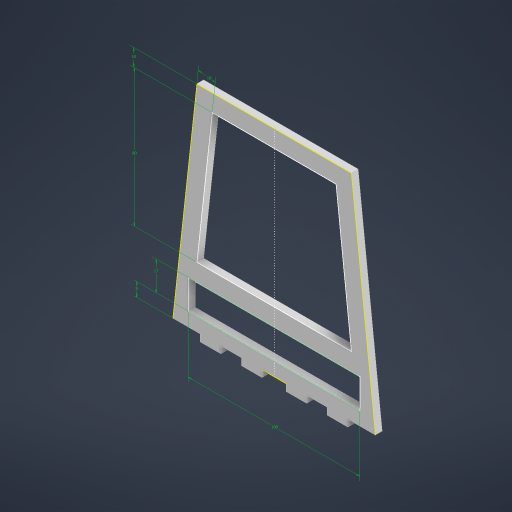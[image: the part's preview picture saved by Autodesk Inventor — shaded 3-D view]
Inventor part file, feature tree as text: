
AUTODESK INVENTOR PART (.ipt)
format: ipt  version: 2023.2 (Build 272271000, 271)  size: 274,944 bytes
history: native  units: mm
features: sketch x2
ambient origin geometry x8: Origin, YZ Plane, XZ Plane, XY Plane, X Axis, Y Axis, Z Axis, Center Point
bodies: Body1 (feature_tree)
feature tree (2):
  sketch  "Sketch1"  dims[d229=90.0mm]
  sketch  "Sketch2"  dims[d232=16.0mm d233=12.0mm d234=12.0mm d235=4.0mm d237=4.0mm d238=0.0mm d239=14.0mm d241=130.0mm d242=100.0mm d243=17.0mm d245=8.0mm d246=10.0mm d247=80.0mm d249=10.0mm d250=4.0mm d251=0.0mm d9=0.5mm d10=0.872665mm d11=0.5mm d12=0.872665mm d13=0.5mm d14=0.872665mm d27=0.5mm d28=0.872665mm d29=0.5mm d30=0.872665mm d88=0.5mm d89=0.872665mm d90=0.5mm d91=0.872665mm d116=0.5mm d117=0.872665mm d118=0.5mm d119=0.872665mm d154=0.5mm d155=0.872665mm d156=0.5mm d157=0.872665mm d181=0.5mm d182=0.872665mm d183=0.5mm d184=0.872665mm d221=0.5mm d222=0.872665mm d223=0.5mm d224=0.872665mm]
